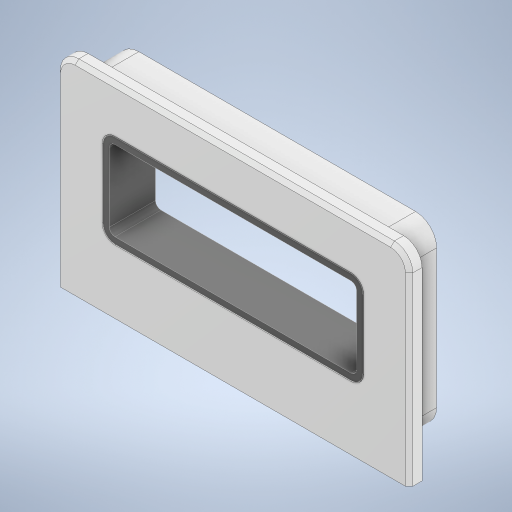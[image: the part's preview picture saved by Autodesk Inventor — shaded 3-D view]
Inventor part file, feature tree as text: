
AUTODESK INVENTOR PART (.ipt)
format: ipt  version: 2024 (Build 280153000, 153)  size: 482,304 bytes
history: native  units: mm
features: sketch x9, extrude x8, projected_geometry x6, fillet x3, plane x3, hole x2, chamfer x1, other x1
ambient origin geometry x8: Origin, YZ Plane, XZ Plane, XY Plane, X Axis, Y Axis, Z Axis, Center Point
bodies: Solid1 (feature_tree)
feature tree (33):
  extrude  "Extrusion1"  Depth=75.0mm
  extrude  "Extrusion2"  Depth=8.0mm TaperAngle=0.0deg
  extrude  "Extrusion3"  Depth=16.0mm
  fillet  "Fillet1"  Radius=50.0mm
  extrude  "Extrusion4"  TaperAngle=15.0deg  [1 undecoded]
  plane  "Work Plane1"
  sketch  "Sketch5"  dims[d13=10.0mm d14=0.0mm d15=3.0mm]
  hole  "Hole1"  [1 undecoded]
  hole  "Hole2"  [1 undecoded]
  extrude  "Extrusion5"  Depth=8.25mm
  fillet  "Fillet2"  Radius=25.0mm
  extrude  "Extrusion6"  Depth=8.25mm
  plane  "Work Plane2"
  extrude  "Extrusion8"  Depth=13.35mm
  fillet  "Fillet3"  Radius=3.0mm
  chamfer  "Chamfer3"  Distance=10.0mm
  plane  "Work Plane3"
  extrude  "Extrusion9"  Depth=8.25mm
  sketch  "Sketch1"  dims[d0=150.0mm d1=75.0mm]
  sketch  "Sketch2"  dims[d3=8.0mm d4=25.0mm d5=0.0mm]
  sketch  "Sketch3"  dims[d6=16.0mm d7=16.0mm d8=50.0mm]
  sketch  "Sketch4"  dims[d10=0.0mm d11=0.0mm d12=15.0deg]
  projected_geometry  "Projected Loop1"
  sketch  "Sketch6"  dims[d16=3.5mm d17=3.4mm d18=0.0mm]
  projected_geometry  "Projected Loop2"
  other  "COVER"
  sketch  "Sketch7"  dims[d19=-8.0mm]
  projected_geometry  "Projected Loop3"
  projected_geometry  "Projected Loop4"
  sketch  "Sketch9"  dims[d20=5.4mm d21=6.0mm d22=4.0mm d23=2.0mm d24=90.0deg d25=8.0mm d26=20.594885mm]
  projected_geometry  "Projected Loop6"
  sketch  "Sketch11"  dims[d27=9.5mm d28=6.0mm d29=4.0mm d30=2.0mm d31=90.0deg d32=8.0mm d33=20.594885mm d34=0.4mm d35=25.0mm d36=25.0mm d37=13.35mm d38=3.0mm d39=0.0mm d40=10.0mm d41=0.4mm d42=4.0mm d43=0.0mm d52=3.0mm d53=4.0mm d54=0.0mm d55=2.0mm d56=2.0mm d57=2.0mm d58=45.0deg d59=-1.0mm d60=8.25mm d61=1.5mm d62=0.0mm d63=20.0mm d64=0.0mm d65=-11.0mm]
  projected_geometry  "Project Cut Edges1"
note: 3 required parameter values undecoded (feature->parameter linkage not recoverable at this tier; creation-order binding heuristic only, values carry confidence <= 0.55)
